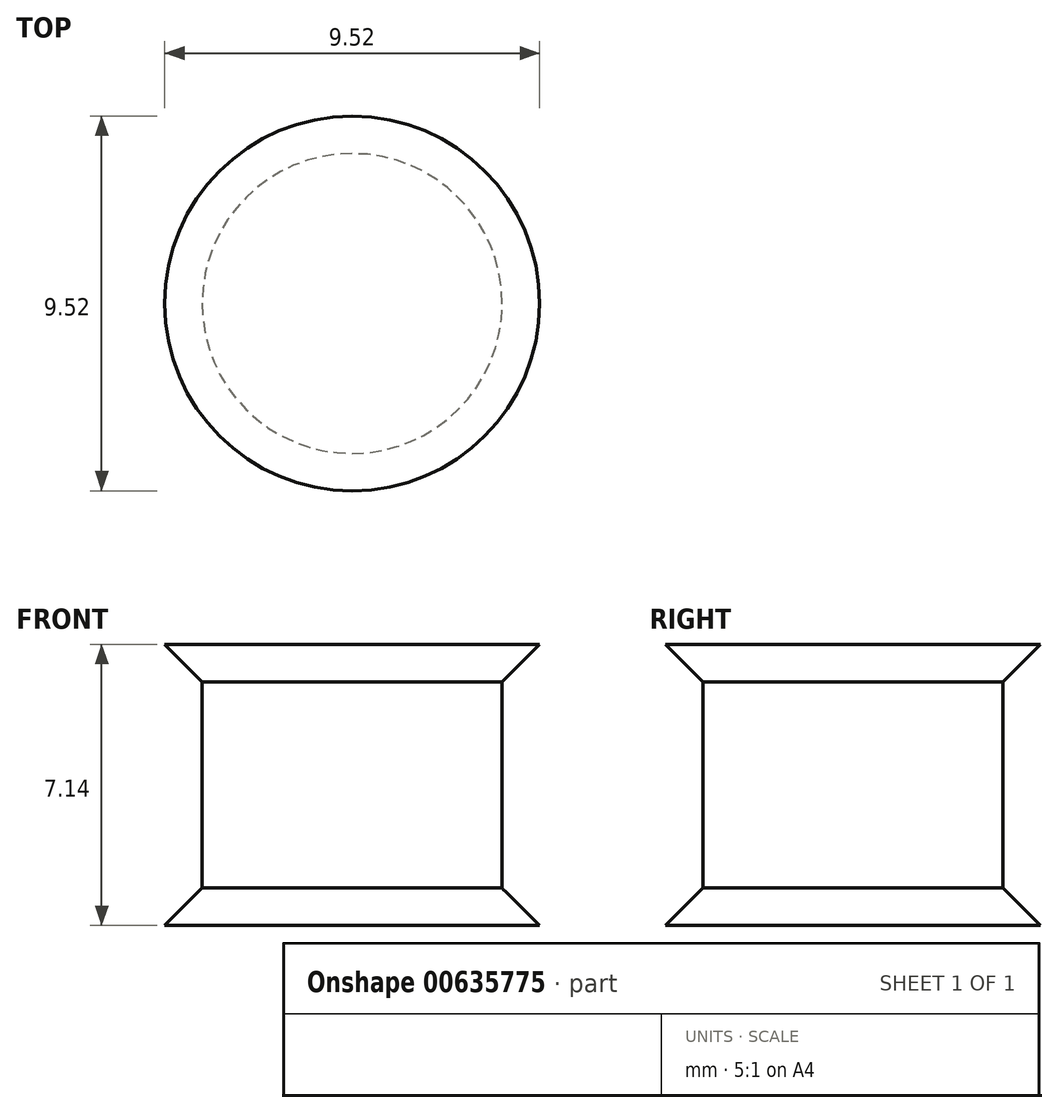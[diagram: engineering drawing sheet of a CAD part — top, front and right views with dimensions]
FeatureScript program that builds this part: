
annotation { "Feature Type Name" : "Feature", "Feature Type Description" : "" }
export const myFeature = defineFeature(function(context is Context, id is Id, definition is map)
    precondition{}
    {
        {
            var Q0;
            Q0=qCreatedBy(makeId("Right.planeOp"),FACE);
            var sketch = newSketch(context, id + "F0", { "sketchPlane" : qUnion([Q0])});
            skLineSegment(sketch, "E0", {"start": v(0, 0) * mm, "end": v(-4.76, 0) * mm});
            skLineSegment(sketch, "E1", {"start": v(-4.76, 0) * mm, "end": v(-3.81, -0.95) * mm});
            skLineSegment(sketch, "E2", {"start": v(-3.81, -0.95) * mm, "end": v(-3.8, -6.2) * mm});
            skLineSegment(sketch, "E3", {"start": v(-3.81, -6.2) * mm, "end": v(-4.76, -7.14) * mm});
            skLineSegment(sketch, "E4", {"start": v(-4.76, -7.14) * mm, "end": v(0, -7.14) * mm});
            skLineSegment(sketch, "E5", {"start": v(0, 0) * mm, "end": v(0, -7.14) * mm});
            skSolve(sketch);
        }
        {
            var Q0;
            Q0=makeQuery(id+"F0.imprint","IMPRINT",FACE,{"disambiguationData":[TD([[makeQuery(id+"F0.imprint","IMPRINT",EDGE,{"derivedFrom":sQuery(id+"F0.wireOp",EDGE,"E0")}),1.0]])]});
            var Q1;
            Q1=sQuery(id+"F0.wireOp",EDGE,"E5");
            revolve(context, id + "F1", {"entities" : qUnion([Q0]), "axis" : qUnion([Q1]), "revolveType" : RevolveType.FULL});
        }
    });
